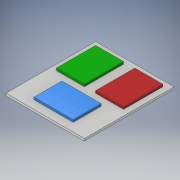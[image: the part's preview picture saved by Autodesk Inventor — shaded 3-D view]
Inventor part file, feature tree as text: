
AUTODESK INVENTOR PART (.ipt)
format: ipt  version: 2018 (Build 220112000, 112)  size: 135,168 bytes
history: native  units: in
note: dims shown in document units (in); Inventor stores cm internally (conversion verified against a paired STEP export)
features: sketch x3, extrude x2
ambient origin geometry x8: Origin, YZ Plane, XZ Plane, XY Plane, X Axis, Y Axis, Z Axis, Center Point
bodies: Solid1 (feature_tree)
feature tree (5):
  extrude  "Extrusion1"  Depth=5.5118in
  sketch  "Sketch2"  dims[d2=0.1575in d3=0.0in d4=1.9685in]
  extrude  "Extrusion2"  Depth=1.9685in
  sketch  "Sketch1"  dims[d0=6.2992in d1=5.5118in]
  sketch  "Sketch3"  dims[d5=2.7559in d6=1.9685in d7=1.9685in d8=2.7559in d9=2.7559in d10=0.5906in d11=0.3937in d12=0.3937in d13=0.3937in d14=0.3937in d15=1.378in d16=1.378in d17=0.1575in d18=0.0in]
